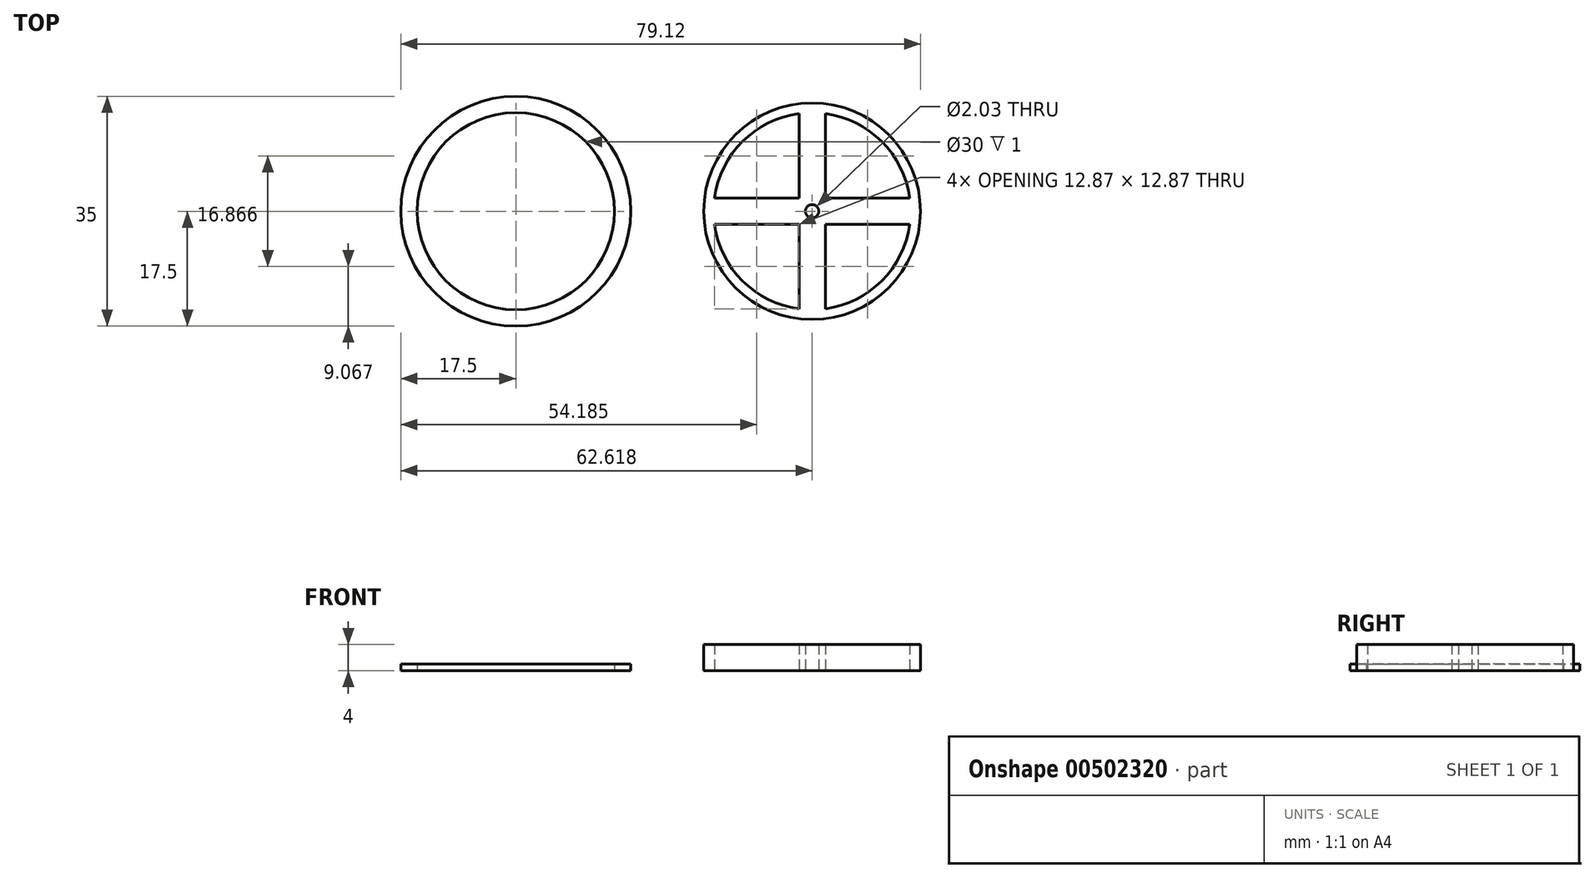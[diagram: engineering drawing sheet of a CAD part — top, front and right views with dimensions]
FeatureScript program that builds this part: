
annotation { "Feature Type Name" : "Feature", "Feature Type Description" : "" }
export const myFeature = defineFeature(function(context is Context, id is Id, definition is map)
    precondition{}
    {
        {
            var Q0;
            Q0=qCreatedBy(makeId("Top.planeOp"),FACE);
            var sketch = newSketch(context, id + "F0", { "sketchPlane" : qUnion([Q0])});
            skCircle(sketch, "E0", {"center": v(0, 0) * mm, "radius": 17.5 * mm});
            skCircle(sketch, "E1", {"center": v(0, 0) * mm, "radius": 15 * mm});
            skArc(sketch, "E2", {"start": v(30.25, -2) * mm, "mid": v(34.51, -10.6) * mm, "end": v(43.12, -14.87) * mm});
            skCircle(sketch, "E3", {"center": v(45.12, 0) * mm, "radius": 16.5 * mm});
            skLineSegment(sketch, "E4", {"start": v(45.12, 15) * mm, "end": v(45.12, -15) * mm, "construction": true});
            skLineSegment(sketch, "E5", {"start": v(30.12, 0) * mm, "end": v(60.12, 0) * mm, "construction": true});
            skLineSegment(sketch, "E6.0", {"start": v(43.12, 14.87) * mm, "end": v(43.12, 2) * mm});
            skLineSegment(sketch, "E7.0", {"start": v(47.12, 14.87) * mm, "end": v(47.12, 2) * mm});
            skLineSegment(sketch, "E8.0", {"start": v(30.25, -2) * mm, "end": v(43.12, -2) * mm});
            skLineSegment(sketch, "E9.0", {"start": v(30.25, 2) * mm, "end": v(43.12, 2) * mm});
            skArc(sketch, "E10.trimOffspring", {"start": v(43.12, 14.87) * mm, "mid": v(34.51, 10.6) * mm, "end": v(30.25, 2) * mm});
            skArc(sketch, "E11.trimOffspring", {"start": v(59.98, 2) * mm, "mid": v(55.72, 10.6) * mm, "end": v(47.12, 14.87) * mm});
            skArc(sketch, "E12.trimOffspring", {"start": v(47.12, -14.87) * mm, "mid": v(55.72, -10.6) * mm, "end": v(59.98, -2) * mm});
            skLineSegment(sketch, "E13.trimOffspring", {"start": v(47.12, 2) * mm, "end": v(59.98, 2) * mm});
            skLineSegment(sketch, "E14.trimOffspring", {"start": v(47.12, -2) * mm, "end": v(47.12, -14.87) * mm});
            skLineSegment(sketch, "E15.trimOffspring", {"start": v(47.12, -2) * mm, "end": v(59.98, -2) * mm});
            skLineSegment(sketch, "E16.trimOffspring", {"start": v(43.12, -2) * mm, "end": v(43.12, -14.87) * mm});
            skCircle(sketch, "E17", {"center": v(45.12, 0) * mm, "radius": 1.02 * mm});
            skSolve(sketch);
        }
        {
            var Q0;
            Q0=makeQuery(id+"F0.imprint","IMPRINT",FACE,{"disambiguationData":[TD([[makeQuery(id+"F0.imprint","IMPRINT",EDGE,{"derivedFrom":sQuery(id+"F0.wireOp",EDGE,"E0")}),1.0]])]});
            extrude(context, id + "F1", {"entities" : qUnion([Q0]), "depth" : 1 * mm});
        }
        {
            var Q0;
            Q0=makeQuery(id+"F0.imprint","IMPRINT",FACE,{"disambiguationData":[TD([[makeQuery(id+"F0.imprint","IMPRINT",EDGE,{"derivedFrom":sQuery(id+"F0.wireOp",EDGE,"E2")}),-1.0]])]});
            extrude(context, id + "F2", {"entities" : qUnion([Q0]), "depth" : 4 * mm});
        }
    });
